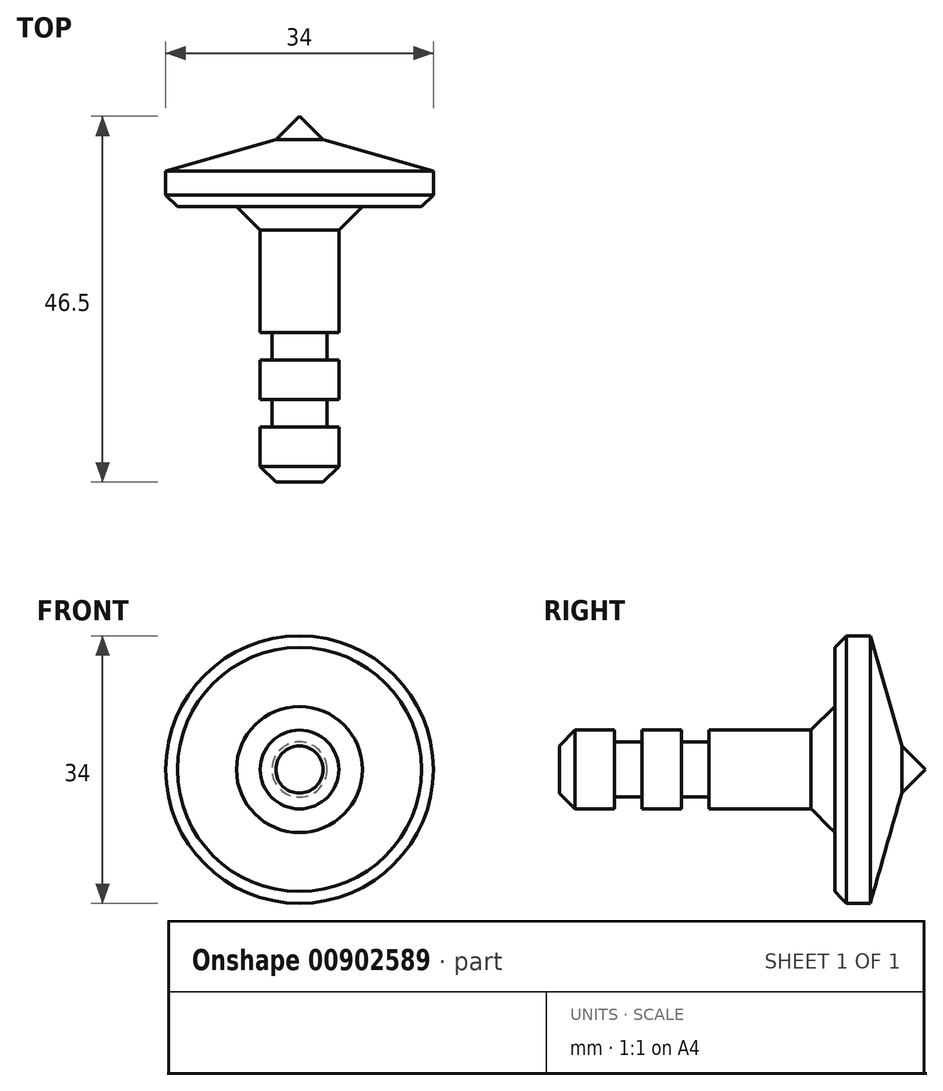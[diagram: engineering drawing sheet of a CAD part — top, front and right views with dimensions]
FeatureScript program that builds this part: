
annotation { "Feature Type Name" : "Feature", "Feature Type Description" : "" }
export const myFeature = defineFeature(function(context is Context, id is Id, definition is map)
    precondition{}
    {
        {
            var Q0;
            Q0=qCreatedBy(makeId("Right.planeOp"),FACE);
            var sketch = newSketch(context, id + "F0", { "sketchPlane" : qUnion([Q0])});
            skLineSegment(sketch, "E0", {"start": v(-7, 17) * mm, "end": v(-10, 17) * mm});
            skLineSegment(sketch, "E1", {"start": v(-10, 17) * mm, "end": v(-11.5, 15.5) * mm});
            skLineSegment(sketch, "E2", {"start": v(-27.5, 5) * mm, "end": v(-27.5, 3.5) * mm});
            skLineSegment(sketch, "E3", {"start": v(-27.5, 3.5) * mm, "end": v(-31, 3.5) * mm});
            skLineSegment(sketch, "E4", {"start": v(-31, 3.5) * mm, "end": v(-31, 5) * mm});
            skLineSegment(sketch, "E5", {"start": v(-31, 5) * mm, "end": v(-36, 5) * mm});
            skLineSegment(sketch, "E6", {"start": v(-36, 5) * mm, "end": v(-36, 3.5) * mm});
            skLineSegment(sketch, "E7", {"start": v(-36, 3.5) * mm, "end": v(-39.5, 3.5) * mm});
            skLineSegment(sketch, "E8", {"start": v(-39.5, 3.5) * mm, "end": v(-39.5, 5) * mm});
            skLineSegment(sketch, "E9", {"start": v(-39.5, 5) * mm, "end": v(-44.5, 5) * mm});
            skLineSegment(sketch, "E10", {"start": v(-44.5, 5) * mm, "end": v(-46.5, 3) * mm});
            skLineSegment(sketch, "E11", {"start": v(-46.5, 3) * mm, "end": v(-46.5, 0) * mm});
            skLineSegment(sketch, "E12", {"start": v(-46.5, 0) * mm, "end": v(0, 0) * mm});
            skLineSegment(sketch, "E13", {"start": v(-7, 17) * mm, "end": v(-3, 3) * mm});
            skLineSegment(sketch, "E14", {"start": v(-3, 3) * mm, "end": v(0, 0) * mm});
            skLineSegment(sketch, "E15", {"start": v(-11.5, 8) * mm, "end": v(-14.5, 5) * mm});
            skLineSegment(sketch, "E16", {"start": v(-14.5, 5) * mm, "end": v(-27.5, 5) * mm});
            skLineSegment(sketch, "E17", {"start": v(-11.5, 15.5) * mm, "end": v(-11.5, 8) * mm});
            skSolve(sketch);
        }
        {
            var Q0;
            Q0 = qSketchRegion(id + "F0", true);
            var Q1;
            Q1=sQuery(id+"F0.wireOp",EDGE,"E12");
            revolve(context, id + "F1", {"surfaceOperationType" : NewSurfaceOperationType.NEW, "entities" : qUnion([Q0]), "axis" : qUnion([Q1]), "revolveType" : RevolveType.FULL});
        }
    });
